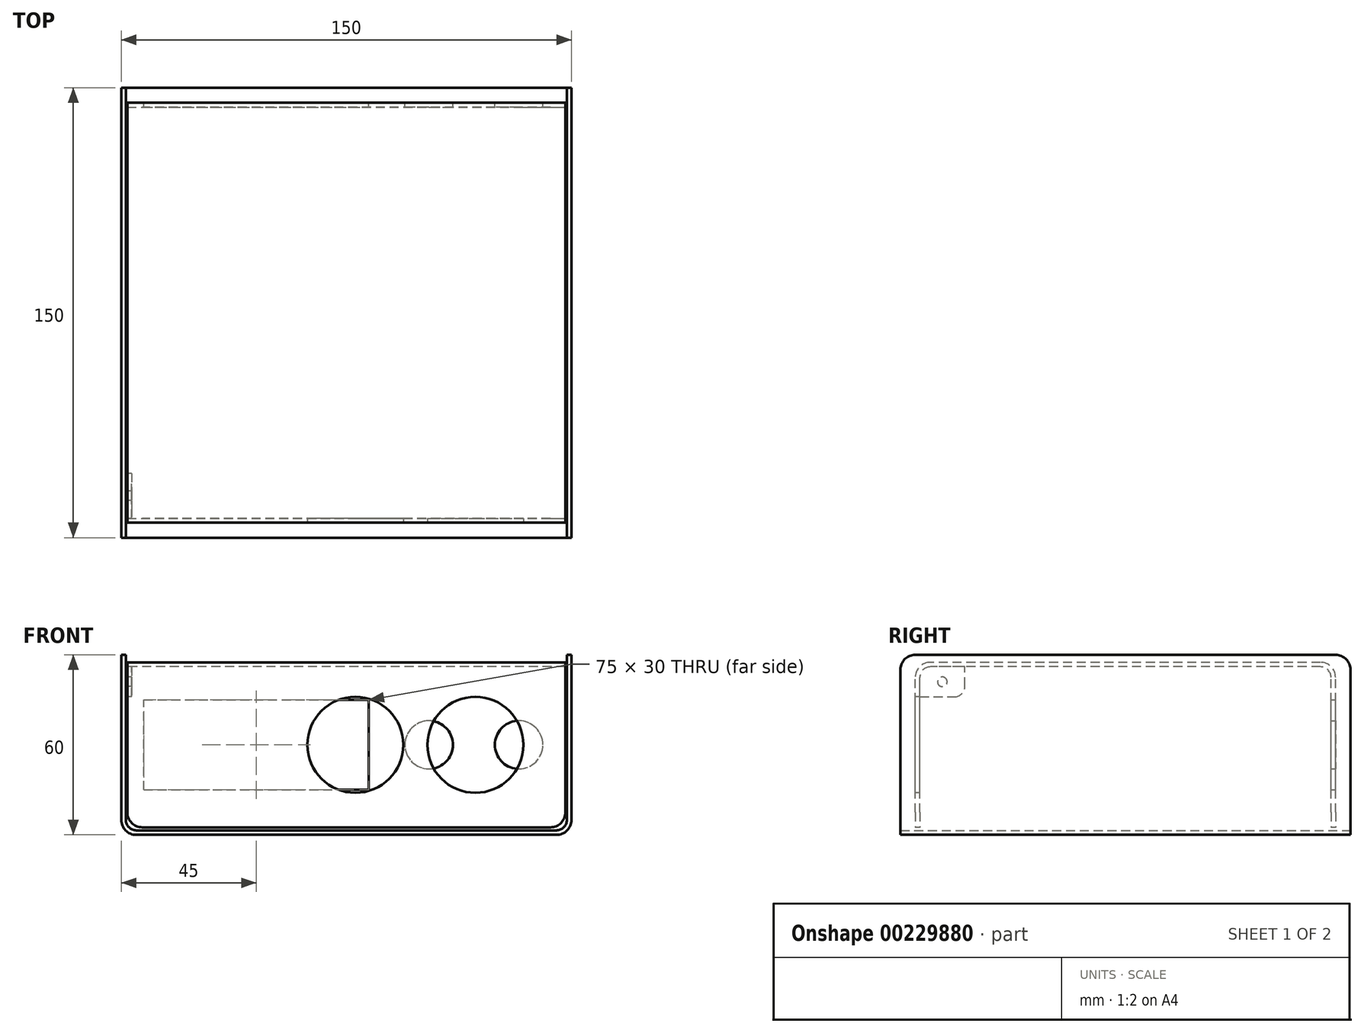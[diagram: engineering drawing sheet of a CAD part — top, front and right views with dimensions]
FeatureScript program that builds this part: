
annotation { "Feature Type Name" : "Feature", "Feature Type Description" : "" }
export const myFeature = defineFeature(function(context is Context, id is Id, definition is map)
    precondition{}
    {
        {
            var Q0;
            Q0=qCreatedBy(makeId("Front.planeOp"),FACE);
            var sketch = newSketch(context, id + "F0", { "sketchPlane" : qUnion([Q0])});
            skLineSegment(sketch, "E0.bottom", {"start": v(75, 30) * mm, "end": v(-75, 30) * mm});
            skLineSegment(sketch, "E0.top", {"start": v(75, -30) * mm, "end": v(-75, -30) * mm});
            skLineSegment(sketch, "E0.left", {"start": v(75, 30) * mm, "end": v(75, -30) * mm});
            skLineSegment(sketch, "E0.right", {"start": v(-75, 30) * mm, "end": v(-75, -30) * mm});
            skPoint(sketch, "E0.middle", {"position": v(0, 0) * mm});
            skSolve(sketch);
        }
        {
            var Q0;
            Q0=makeQuery(id+"F0.imprint","IMPRINT",FACE,{"disambiguationData":[TD([[makeQuery(id+"F0.imprint","IMPRINT",EDGE,{"derivedFrom":sQuery(id+"F0.wireOp",EDGE,"E0.bottom")}),1.0]])]});
            extrude(context, id + "F1", {"entities" : qUnion([Q0]), "depth" : 75 * mm, "hasSecondDirection" : true, "secondDirectionOppositeDirection" : true, "secondDirectionDepth" : 75 * mm});
        }
        {
            var Q0;
            Q0=makeQuery(id+"F1.opExtrude","SWEPT_EDGE",EDGE,{"disambiguationData":[OSD([sQuery(id+"F0.wireOp",EDGE,"E0.top"),sQuery(id+"F0.wireOp",EDGE,"E0.left")])]});
            var Q1;
            Q1=makeQuery(id+"F1.opExtrude","SWEPT_EDGE",EDGE,{"disambiguationData":[OSD([sQuery(id+"F0.wireOp",EDGE,"E0.top"),sQuery(id+"F0.wireOp",EDGE,"E0.right")])]});
            fillet(context, id + "F2", {"entities" : qUnion([Q0, Q1]), "radius" : 5 * mm, "tangentPropagation" : true, "allowEdgeOverflow" : false});
        }
        {
            var Q0;
            Q0=makeQuery(id+"F1.opExtrude","CAP_FACE",FACE,{"disambiguationData":[OSD([sQuery(id+"F0.wireOp",EDGE,"E0.bottom"),sQuery(id+"F0.wireOp",EDGE,"E0.top"),sQuery(id+"F0.wireOp",EDGE,"E0.left"),sQuery(id+"F0.wireOp",EDGE,"E0.right")])],"isStart":true});
            var Q1;
            Q1=makeQuery(id+"F1.opExtrude","CAP_FACE",FACE,{"disambiguationData":[OSD([sQuery(id+"F0.wireOp",EDGE,"E0.bottom"),sQuery(id+"F0.wireOp",EDGE,"E0.top"),sQuery(id+"F0.wireOp",EDGE,"E0.left"),sQuery(id+"F0.wireOp",EDGE,"E0.right")])],"isStart":false});
            var Q2;
            Q2=makeQuery(id+"F1.opExtrude","SWEPT_FACE",FACE,{"disambiguationData":[OSD([sQuery(id+"F0.wireOp",EDGE,"E0.bottom")])]});
            shell(context, id + "F3", {"entities" : qUnion([Q0, Q1, Q2]), "thickness" : 1.5 * mm});
        }
        {
            var Q0;
            {var subQ0=sQuery(id+"F0.wireOp",EDGE,"E0.bottom");Q0=makeQuery(id+"F3.opShell","OFFSET_EDGE",EDGE,{"disambiguationData":[OSD([subQ0]),TDD([makeQuery(id+"F1.opExtrude","CAP_EDGE",EDGE,{"disambiguationData":[OSD([subQ0])],"isStart":false})])]});}
            var Q1;
            {var subQ0=sQuery(id+"F0.wireOp",EDGE,"E0.bottom");Q1=makeQuery(id+"F3.opShell","OFFSET_EDGE",EDGE,{"disambiguationData":[OSD([subQ0]),TDD([makeQuery(id+"F1.opExtrude","CAP_EDGE",EDGE,{"disambiguationData":[OSD([subQ0])],"isStart":true})])]});}
            var Q2;
            Q2=makeQuery(id+"F1.opExtrude","CAP_EDGE",EDGE,{"disambiguationData":[OSD([sQuery(id+"F0.wireOp",EDGE,"E0.bottom")])],"isStart":false});
            var Q3;
            Q3=makeQuery(id+"F1.opExtrude","CAP_EDGE",EDGE,{"disambiguationData":[OSD([sQuery(id+"F0.wireOp",EDGE,"E0.bottom")])],"isStart":true});
            fillet(context, id + "F4", {"entities" : qUnion([Q0, Q1, Q2, Q3]), "radius" : 5 * mm, "tangentPropagation" : true, "allowEdgeOverflow" : false});
        }
        {
            var Q0;
            Q0=qCreatedBy(makeId("Right.planeOp"),FACE);
            var sketch = newSketch(context, id + "F5", { "sketchPlane" : qUnion([Q0])});
            skLineSegment(sketch, "E1.bottom", {"start": v(70, -27.5) * mm, "end": v(-70, -27.5) * mm});
            skLineSegment(sketch, "E1.top", {"start": v(70, 27.5) * mm, "end": v(-70, 27.5) * mm});
            skLineSegment(sketch, "E1.left", {"start": v(70, -27.5) * mm, "end": v(70, 27.5) * mm});
            skLineSegment(sketch, "E1.right", {"start": v(-70, -27.5) * mm, "end": v(-70, 27.5) * mm});
            skPoint(sketch, "E1.middle", {"position": v(0, 0) * mm});
            skSolve(sketch);
        }
        {
            var Q0;
            Q0=makeQuery(id+"F5.imprint","IMPRINT",FACE,{"disambiguationData":[TD([[makeQuery(id+"F5.imprint","IMPRINT",EDGE,{"derivedFrom":sQuery(id+"F5.wireOp",EDGE,"E1.bottom")}),-1.0]])]});
            extrude(context, id + "F6", {"entities" : qUnion([Q0]), "depth" : 73 * mm, "hasSecondDirection" : true, "secondDirectionOppositeDirection" : true, "secondDirectionDepth" : 73 * mm});
        }
        {
            var Q0;
            Q0=makeQuery(id+"F6.opExtrude","SWEPT_EDGE",EDGE,{"disambiguationData":[OSD([sQuery(id+"F5.wireOp",EDGE,"E1.top"),sQuery(id+"F5.wireOp",EDGE,"E1.right")])]});
            var Q1;
            Q1=makeQuery(id+"F6.opExtrude","SWEPT_EDGE",EDGE,{"disambiguationData":[OSD([sQuery(id+"F5.wireOp",EDGE,"E1.top"),sQuery(id+"F5.wireOp",EDGE,"E1.left")])]});
            fillet(context, id + "F7", {"entities" : qUnion([Q0, Q1]), "radius" : 5 * mm, "tangentPropagation" : true, "allowEdgeOverflow" : false});
        }
        {
            var Q0;
            Q0=makeQuery(id+"F6.opExtrude","SWEPT_FACE",FACE,{"disambiguationData":[OSD([sQuery(id+"F5.wireOp",EDGE,"E1.bottom")])]});
            var Q1;
            Q1=makeQuery(id+"F6.opExtrude","CAP_FACE",FACE,{"disambiguationData":[OSD([sQuery(id+"F5.wireOp",EDGE,"E1.bottom"),sQuery(id+"F5.wireOp",EDGE,"E1.top"),sQuery(id+"F5.wireOp",EDGE,"E1.left"),sQuery(id+"F5.wireOp",EDGE,"E1.right")])],"isStart":false});
            var Q2;
            Q2=makeQuery(id+"F6.opExtrude","CAP_FACE",FACE,{"disambiguationData":[OSD([sQuery(id+"F5.wireOp",EDGE,"E1.bottom"),sQuery(id+"F5.wireOp",EDGE,"E1.top"),sQuery(id+"F5.wireOp",EDGE,"E1.left"),sQuery(id+"F5.wireOp",EDGE,"E1.right")])],"isStart":true});
            shell(context, id + "F8", {"entities" : qUnion([Q0, Q1, Q2]), "thickness" : 1.5 * mm});
        }
        {
            var Q0;
            Q0=makeQuery(id+"F6.opExtrude","CAP_EDGE",EDGE,{"disambiguationData":[OSD([sQuery(id+"F5.wireOp",EDGE,"E1.bottom")])],"isStart":false});
            var Q1;
            Q1=makeQuery(id+"F6.opExtrude","CAP_EDGE",EDGE,{"disambiguationData":[OSD([sQuery(id+"F5.wireOp",EDGE,"E1.bottom")])],"isStart":true});
            var Q2;
            {var subQ0=sQuery(id+"F5.wireOp",EDGE,"E1.bottom");Q2=makeQuery(id+"F8.opShell","OFFSET_EDGE",EDGE,{"disambiguationData":[OSD([subQ0]),TDD([makeQuery(id+"F6.opExtrude","CAP_EDGE",EDGE,{"disambiguationData":[OSD([subQ0])],"isStart":false})])]});}
            var Q3;
            {var subQ0=sQuery(id+"F5.wireOp",EDGE,"E1.bottom");Q3=makeQuery(id+"F8.opShell","OFFSET_EDGE",EDGE,{"disambiguationData":[OSD([subQ0]),TDD([makeQuery(id+"F6.opExtrude","CAP_EDGE",EDGE,{"disambiguationData":[OSD([subQ0])],"isStart":true})])]});}
            fillet(context, id + "F9", {"entities" : qUnion([Q0, Q1, Q2, Q3]), "radius" : 5 * mm, "tangentPropagation" : true, "allowEdgeOverflow" : false});
        }
        {
            var Q0;
            Q0=makeQuery(id+"F6.opExtrude","SWEPT_FACE",FACE,{"disambiguationData":[OSD([sQuery(id+"F5.wireOp",EDGE,"E1.left")])]});
            var sketch = newSketch(context, id + "F10", { "sketchPlane" : qUnion([Q0])});
            skLineSegment(sketch, "E2.bottom", {"start": v(67.5, -15) * mm, "end": v(-7.5, -15) * mm});
            skLineSegment(sketch, "E2.top", {"start": v(67.5, 15) * mm, "end": v(-7.5, 15) * mm});
            skLineSegment(sketch, "E2.left", {"start": v(67.5, -15) * mm, "end": v(67.5, 15) * mm});
            skLineSegment(sketch, "E2.right", {"start": v(-7.5, -15) * mm, "end": v(-7.5, 15) * mm});
            skPoint(sketch, "E2.middle", {"position": v(30, 0) * mm});
            skSolve(sketch);
        }
        {
            var Q0;
            Q0=makeQuery(id+"F10.imprint","IMPRINT",FACE,{"disambiguationData":[TD([[makeQuery(id+"F10.imprint","IMPRINT",EDGE,{"derivedFrom":sQuery(id+"F10.wireOp",EDGE,"E2.bottom")}),-1.0]])]});
            extrude(context, id + "F11", {"entities" : qUnion([Q0]), "operationType" : NewBodyOperationType.REMOVE, "endBound" : BoundingType.UP_TO_NEXT, "oppositeDirection" : true, "depth" : 25 * mm});
        }
        {
            var Q0;
            Q0=makeQuery(id+"F6.opExtrude","SWEPT_FACE",FACE,{"disambiguationData":[OSD([sQuery(id+"F5.wireOp",EDGE,"E1.left")])]});
            var sketch = newSketch(context, id + "F12", { "sketchPlane" : qUnion([Q0])});
            skPoint(sketch, "E3", {"position": v(-27.5, 0) * mm});
            skPoint(sketch, "E4", {"position": v(-57.5, 0) * mm});
            skSolve(sketch);
        }
        {
            var Q0;
            Q0=sQuery(id+"F12.wireOp",VERTEX,"E3");
            var Q1;
            Q1=sQuery(id+"F12.wireOp",VERTEX,"E4");
            var Q2;
            Q2=makeQuery(id+"F6.opExtrude","SWEPT_BODY",BODY,{"disambiguationData":[OSD([sQuery(id+"F5.wireOp",EDGE,"E1.bottom"),sQuery(id+"F5.wireOp",EDGE,"E1.top"),sQuery(id+"F5.wireOp",EDGE,"E1.left"),sQuery(id+"F5.wireOp",EDGE,"E1.right")])]});
            hole(context, id + "F13", {"style" : HoleStyle.SIMPLE, "endStyle" : HoleEndStyle.BLIND, "holeDiameter" : 16 * mm, "holeDepth" : 5 * mm, "locations" : qUnion([Q0, Q1]), "scope" : qUnion([Q2])});
        }
        {
            var Q0;
            Q0=makeQuery(id+"F6.opExtrude","SWEPT_FACE",FACE,{"disambiguationData":[OSD([sQuery(id+"F5.wireOp",EDGE,"E1.right")])]});
            var sketch = newSketch(context, id + "F14", { "sketchPlane" : qUnion([Q0])});
            skPoint(sketch, "E5", {"position": v(43, 0) * mm});
            skPoint(sketch, "E6", {"position": v(3, 0) * mm});
            skSolve(sketch);
        }
        {
            var Q0;
            Q0=sQuery(id+"F14.wireOp",VERTEX,"E5");
            var Q1;
            Q1=sQuery(id+"F14.wireOp",VERTEX,"E6");
            var Q2;
            Q2=makeQuery(id+"F6.opExtrude","SWEPT_BODY",BODY,{"disambiguationData":[OSD([sQuery(id+"F5.wireOp",EDGE,"E1.bottom"),sQuery(id+"F5.wireOp",EDGE,"E1.top"),sQuery(id+"F5.wireOp",EDGE,"E1.left"),sQuery(id+"F5.wireOp",EDGE,"E1.right")])]});
            hole(context, id + "F15", {"style" : HoleStyle.SIMPLE, "endStyle" : HoleEndStyle.BLIND, "holeDiameter" : 32 * mm, "holeDepth" : 5 * mm, "locations" : qUnion([Q0, Q1]), "scope" : qUnion([Q2])});
        }
        {
            var Q0;
            Q0=makeQuery(id+"F6.opExtrude","CAP_FACE",FACE,{"disambiguationData":[OSD([sQuery(id+"F5.wireOp",EDGE,"E1.bottom"),sQuery(id+"F5.wireOp",EDGE,"E1.top"),sQuery(id+"F5.wireOp",EDGE,"E1.left"),sQuery(id+"F5.wireOp",EDGE,"E1.right")])],"isStart":true});
            var sketch = newSketch(context, id + "F16", { "sketchPlane" : qUnion([Q0])});
            skLineSegment(sketch, "E7.bottom", {"start": v(68.5, 16) * mm, "end": v(57, 16) * mm});
            skLineSegment(sketch, "E7.top", {"start": v(65, 26) * mm, "end": v(53.5, 26) * mm});
            skLineSegment(sketch, "E7.left", {"start": v(68.5, 16) * mm, "end": v(68.5, 22.5) * mm});
            skLineSegment(sketch, "E7.right", {"start": v(53.5, 19.5) * mm, "end": v(53.5, 26) * mm});
            skPoint(sketch, "E8.visualSharp", {"position": v(68.5, 26) * mm});
            skArc(sketch, "E8.filletArc", {"start": v(68.5, 22.5) * mm, "mid": v(67.47, 24.97) * mm, "end": v(65, 26) * mm});
            skPoint(sketch, "E9.visualSharp", {"position": v(53.5, 16) * mm});
            skArc(sketch, "E9.filletArc", {"start": v(53.5, 19.5) * mm, "mid": v(54.53, 17.03) * mm, "end": v(57, 16) * mm});
            skSolve(sketch);
        }
        {
            var Q0;
            Q0=makeQuery(id+"F16.imprint","IMPRINT",FACE,{"disambiguationData":[TD([[makeQuery(id+"F16.imprint","IMPRINT",EDGE,{"derivedFrom":sQuery(id+"F16.wireOp",EDGE,"E7.bottom")}),-1.0]])]});
            extrude(context, id + "F17", {"entities" : qUnion([Q0]), "oppositeDirection" : true, "depth" : 1.5 * mm});
        }
        {
            var Q0;
            Q0=makeQuery(id+"F17.opExtrude","CAP_FACE",FACE,{"disambiguationData":[OSD([sQuery(id+"F16.wireOp",EDGE,"E7.bottom"),sQuery(id+"F16.wireOp",EDGE,"E7.top"),sQuery(id+"F16.wireOp",EDGE,"E7.left"),sQuery(id+"F16.wireOp",EDGE,"E7.right"),sQuery(id+"F16.wireOp",EDGE,"E8.filletArc"),sQuery(id+"F16.wireOp",EDGE,"E9.filletArc")])],"isStart":true});
            var sketch = newSketch(context, id + "F18", { "sketchPlane" : qUnion([Q0])});
            skPoint(sketch, "E10", {"position": v(61, 21) * mm});
            skSolve(sketch);
        }
        {
            var Q0;
            Q0=sQuery(id+"F18.wireOp",VERTEX,"E10");
            var Q1;
            Q1=makeQuery(id+"F17.opExtrude","SWEPT_BODY",BODY,{"disambiguationData":[OSD([sQuery(id+"F16.wireOp",EDGE,"E7.bottom"),sQuery(id+"F16.wireOp",EDGE,"E7.top"),sQuery(id+"F16.wireOp",EDGE,"E7.left"),sQuery(id+"F16.wireOp",EDGE,"E7.right"),sQuery(id+"F16.wireOp",EDGE,"E8.filletArc"),sQuery(id+"F16.wireOp",EDGE,"E9.filletArc")])]});
            hole(context, id + "F19", {"style" : HoleStyle.SIMPLE, "endStyle" : HoleEndStyle.BLIND, "standardTappedOrClearance" : lookupTablePath({ "standard" : "ISO", "engagement" : "75%", "pitch" : "0.75 mm", "size" : "M4", "type" : "Tapped" }), "standardBlindInLast" : lookupTablePath({ "standard" : "ISO", "engagement" : "75%", "pitch" : "0.75 mm", "size" : "M4", "type" : "Tapped" }), "holeDiameter" : 3.2 * mm, "holeDepth" : 5 * mm, "locations" : qUnion([Q0]), "scope" : qUnion([Q1])});
        }
    });
